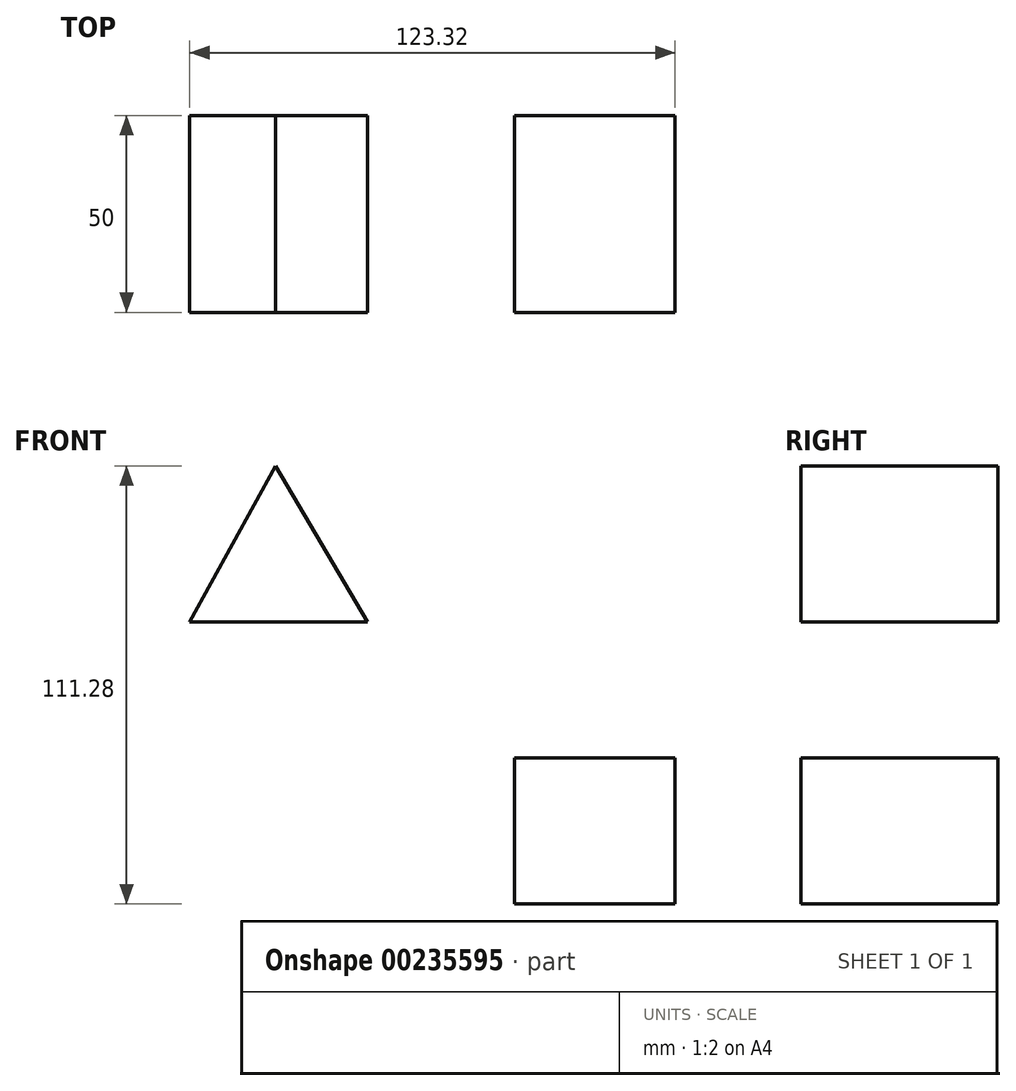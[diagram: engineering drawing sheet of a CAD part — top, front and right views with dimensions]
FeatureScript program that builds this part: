
annotation { "Feature Type Name" : "Feature", "Feature Type Description" : "" }
export const myFeature = defineFeature(function(context is Context, id is Id, definition is map)
    precondition{}
    {
        {
            var Q0;
            Q0=qCreatedBy(makeId("Front.planeOp"),FACE);
            var sketch = newSketch(context, id + "F0", { "sketchPlane" : qUnion([Q0])});
            skLineSegment(sketch, "E0", {"start": v(-58.45, 12.5) * mm, "end": v(-13.2, 12.5) * mm});
            skLineSegment(sketch, "E1", {"start": v(-13.2, 12.5) * mm, "end": v(-36.6, 52.11) * mm});
            skLineSegment(sketch, "E2", {"start": v(-36.6, 52.11) * mm, "end": v(-58.45, 12.5) * mm});
            skFitSpline(sketch, "E3", {"points": [v(-13.2, 12.5) * mm, v(0, 0) * mm, v(7.41, -16.68) * mm, v(23.86, -22) * mm, v(24.32, -22) * mm], "startDerivative": vector(50, -33.62) * mm, "endDerivative": vector(4.91, 0.56) * mm});
            skLineSegment(sketch, "E4.bottom", {"start": v(64.87, -59.17) * mm, "end": v(24.1, -59.17) * mm});
            skLineSegment(sketch, "E4.top", {"start": v(64.87, -22.11) * mm, "end": v(24.1, -22.11) * mm});
            skLineSegment(sketch, "E4.left", {"start": v(64.87, -59.17) * mm, "end": v(64.87, -22.11) * mm});
            skLineSegment(sketch, "E4.right", {"start": v(24.1, -59.17) * mm, "end": v(24.1, -22.11) * mm});
            skPoint(sketch, "E4.middle", {"position": v(44.49, -40.64) * mm});
            skLineSegment(sketch, "E5.bottom", {"start": v(64.87, -22.11) * mm, "end": v(58.85, -22.11) * mm});
            skLineSegment(sketch, "E5.top", {"start": v(64.87, -22.11) * mm, "end": v(58.85, -22.11) * mm});
            skLineSegment(sketch, "E5.left", {"start": v(64.87, -22.11) * mm, "end": v(64.87, -22.11) * mm});
            skLineSegment(sketch, "E5.right", {"start": v(58.85, -22.11) * mm, "end": v(58.85, -22.11) * mm});
            skPoint(sketch, "E5.middle", {"position": v(61.86, -22.11) * mm});
            skSolve(sketch);
        }
        {
            var Q0;
            Q0=makeQuery(id+"F0.imprint","IMPRINT",FACE,{"disambiguationData":[TD([[makeQuery(id+"F0.imprint","IMPRINT",EDGE,{"derivedFrom":sQuery(id+"F0.wireOp",EDGE,"E0")}),1.0]])]});
            var Q1;
            Q1=makeQuery(id+"F0.imprint","IMPRINT",FACE,{"disambiguationData":[TD([[makeQuery(id+"F0.imprint","IMPRINT",EDGE,{"derivedFrom":sQuery(id+"F0.wireOp",EDGE,"E4.bottom")}),-1.0]])]});
            extrude(context, id + "F1", {"entities" : qUnion([Q0, Q1]), "depth" : 50 * mm});
        }
    });
